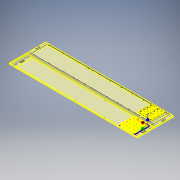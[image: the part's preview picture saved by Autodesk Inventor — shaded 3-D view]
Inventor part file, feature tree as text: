
AUTODESK INVENTOR PART (.ipt)
format: ipt  version: 2018.3 (Build 223284000, 284)  size: 9,961,472 bytes
history: native  units: in
note: dims shown in document units (in); Inventor stores cm internally (conversion verified against a paired STEP export)
features: other x145, extrude x13, projected_geometry x10, pattern_linear x5, hole x3, sketch x2
ambient origin geometry x8: Origin, YZ Plane, XZ Plane, XY Plane, X Axis, Y Axis, Z Axis, Center Point
bodies: Solid61 (feature_tree), Solid62 (feature_tree), Solid63 (feature_tree), Solid64 (feature_tree), Solid89 (feature_tree), Solid161 (feature_tree), Solid162 (feature_tree), Solid171 (feature_tree), Solid173 (feature_tree), Solid174 (feature_tree), Solid176 (feature_tree), Solid177 (feature_tree), Solid242 (feature_tree), Solid244 (feature_tree), Solid246 (feature_tree), Solid247 (feature_tree), Solid248 (feature_tree), Solid249 (feature_tree), Solid250 (feature_tree), Solid272 (feature_tree), Solid273 (feature_tree), Solid274 (feature_tree), Solid275 (feature_tree), Solid276 (feature_tree), Solid298 (feature_tree), Solid299 (feature_tree), Solid300 (feature_tree), Solid301 (feature_tree), Solid302 (feature_tree), Solid372 (feature_tree), Solid378 (feature_tree), Solid379 (feature_tree), Solid385 (feature_tree), Solid386 (feature_tree), Solid488 (feature_tree), Solid489 (feature_tree), Solid490 (feature_tree), Solid491 (feature_tree), Solid492 (feature_tree), Solid493 (feature_tree), Solid494 (feature_tree), Solid495 (feature_tree), Solid609 (feature_tree), Solid611 (feature_tree), Solid608 (feature_tree), Solid610 (feature_tree)
feature tree (178):
  other  "Fixture Assembly.iam"
  other  "Fixture Base.ipt:1"
  other  "Case Top Contour Fixture.ipt:1"
  other  "Case Top Contour Fixture.ipt:2"
  other  "Case Top Contour Fixture.ipt:3"
  other  "Case Top Contour Fixture.ipt:4"
  other  "Case Top Contour Fixture.ipt:5"
  other  "Case Top Contour Fixture.ipt:6"
  other  "Case Bottom Contour Fixture.ipt:16"
  other  "Case Top Pocket Fixture.ipt:1"
  other  "Case Bottom Pocket Fixture.ipt:1"
  other  "Case Top Pocket Fixture.ipt:3"
  other  "Case Top Pocket Fixture.ipt:4"
  other  "Case Top Pocket Fixture.ipt:5"
  other  "Case Top Pocket Fixture.ipt:6"
  other  "Case Top Pocket Fixture.ipt:7"
  other  "Case Bottom Contour Fixture.ipt:17"
  other  "Case Bottom Contour Fixture.ipt:18"
  other  "Case Bottom Contour Fixture.ipt:19"
  other  "Case Bottom Contour Fixture.ipt:20"
  other  "Case Bottom Contour Fixture.ipt:21"
  other  "Case Bottom Pocket Fixture.ipt:2"
  other  "Case Bottom Pocket Fixture.ipt:3"
  other  "Case Bottom Pocket Fixture.ipt:4"
  other  "Case Bottom Pocket Fixture.ipt:5"
  other  "Case Bottom Pocket Fixture.ipt:6"
  other  "Case Top Pocket Fixture.ipt:17"
  other  "Case Top Pocket Fixture.ipt:19"
  other  "Case Top Pocket Fixture.ipt:50"
  other  "Case Bottom Pocket Fixture.ipt:49"
  other  "Case Top Pocket Fixture.ipt:51"
  other  "Case Bottom Pocket Fixture.ipt:50"
  other  "Case Top Contour Fixture.ipt:7"
  other  "Case Bottom Contour Fixture.ipt:22"
  other  "Case Top Contour Fixture.ipt:8"
  other  "Case Bottom Contour Fixture.ipt:23"
  other  "Base Solid"
  other  "Pocket Registration Sketch"
  other  "Contour Registration Sketch"
  extrude  "Pocket Registration Hole"  Depth=0.3937in
  extrude  "Contour Registration Hole"  Depth=0.25in
  other  "Hold-down Plane"
  other  "Hold-down Sketch 1"
  other  "Hold-down Sketch 2"
  extrude  "Hold-down Pocket 1"  TaperAngle=0.0deg  [1 undecoded]
  extrude  "Hold-down Pocket 2"  TaperAngle=0.0deg  [1 undecoded]
  pattern_linear  "Hold-down Pocket Pattern"  Spacing1=0.25in  [1 undecoded]
  other  "Case Top Mount Sketch"
  extrude  "Case Top Mount Outer Extrusion"  Depth=0.55in
  extrude  "Case Top Mount Opening Extrusion"  Depth=0.75in TaperAngle=360.0deg
  extrude  "Case Bottom Mount Extrusion"  Depth=0.75in TaperAngle=0.0deg
  extrude  "Case Top Mount Ejection"  Depth=0.75in TaperAngle=0.0deg
  extrude  "Case Bottom Mount Ejection"  Depth=2.353in
  hole  "Case Bottom Vacuum Hole"  [1 undecoded]
  hole  "Case Top Long-grain Vacuum Hole"  [1 undecoded]
  hole  "Case Top End-grain Vacuum Hole"  [1 undecoded]
  pattern_linear  "Group Pattern"  Spacing1=0.25in  [1 undecoded]
  pattern_linear  "Group Fixture Pattern"  Spacing1=0.25in  [1 undecoded]
  other  "Partial Clean Sketch"
  extrude  "Extrusion43"  Depth=0.25in
  extrude  "Extrusion44"  Depth=0.75in
  pattern_linear  "Rectangular Pattern14"  Spacing1=10.0in  [1 undecoded]
  extrude  "Extrusion45"  Depth=0.75in
  extrude  "Extrusion46"  Depth=0.75in
  pattern_linear  "Rectangular Pattern15"  Spacing1=30.0in  [1 undecoded]
  other  "First Contour Top"
  other  "Origin Sketch"
  other  "Alignment Sketch_1"
  other  "3/16" Vacuum Drill Sketch"
  projected_geometry  "Projected Loop17"
  sketch  "Sketch496"  dims[d16=0.7874in d18=4.706in d29=0.3937in]
  other  "First Contour Bottom"
  other  "Alignment Sketch_56"
  other  "Peg Sketch_45"
  sketch  "Sketch509"  dims[d205=0.55in d206=0.25in d232=0.0in d233=0.0in d234=0.0in d235=0.0in d236=0.25in d237=0.55in d238=1.5748in d240=360.0deg d242=0.08in d243=0.0in d244=0.08in d245=0.0in d246=0.5in d247=0.75in d248=0.375in d249=0.25in d250=0.5635in d251=1.0in d252=0.8108in d253=0.1875in d254=0.75in d255=0.375in d256=0.25in d257=0.5635in d258=1.0in d259=0.8108in d260=0.125in d261=0.75in d262=0.375in d263=0.25in d264=0.5635in d265=1.0in d266=0.8108in d267=1.5748in d269=2.353in d372=0.25in d373=0.25in d374=0.25in d375=0.25in d376=0.25in d377=0.25in d378=10.0in d379=10.0in d380=10.0in d381=20.0in d382=30.0in d383=41.0in d384=10.0in d385=0.25in d390=1.0in d391=0.0in d393=1.0in d402=0.05in d403=0.0in d404=0.05in d405=0.0in d420=0.126in d436=0.025in d437=0.0in d438=3.1496in d440=10.25in d441=0.126in d442=0.025in d443=0.0in d444=0.3937in d446=10.25in d468=0.25in d469=0.25in d473=0.75in d475=1.5748in d477=360.0deg d481=0.25in d482=0.5in d483=0.0in d484=10.0in d485=0.25in d486=0.0in d487=0.5in d488=0.25in d489=0.25in d490=0.25in d491=0.125in d492=0.125in d493=0.0in d494=0.0in d499=0.25in d500=0.05in d501=0.0in d502=3.937in d504=1.0in d505=0.3937in d507=1.0in d509=0.126in d510=5.076in d511=0.126in d512=5.076in d513=0.015in d514=0.0in d515=0.015in d516=0.0in d517=6.2992in d519=5.06in d520=0.25in d521=0.75in d522=0.3818in d523=0.126in d524=7.198in d525=0.023in d526=0.025in d527=0.0in d528=2.7559in d530=7.75in d531=0.75in d532=0.126in d533=7.198in d534=0.7499in d535=0.015in d536=0.0in]
  other  "Pattern of Solid162:9"
  other  "Pattern of Solid162:11"
  other  "Pattern of Solid162:12"
  other  "Pattern of Solid162:14"
  other  "Pattern of Solid162:15"
  other  "New peg sketch_51"
  other  "Alignment Sketch"
  other  "3/16" Vacuum Drill Sketch_36"
  other  "Alignment Sketch_63"
  other  "New peg sketch_53"
  other  "Alignment Sketch_65"
  other  "3/16" Vacuum Drill Sketch_38"
  other  "New peg sketch_54"
  other  "Alignment Sketch_66"
  other  "3/16" Vacuum Drill Sketch_39"
  other  "New peg sketch_55"
  other  "Alignment Sketch_67"
  other  "3/16" Vacuum Drill Sketch_40"
  other  "New peg sketch_56"
  other  "Alignment Sketch_68"
  other  "3/16" Vacuum Drill Sketch_41"
  other  "New peg sketch_57"
  other  "Alignment Sketch_69"
  other  "3/16" Vacuum Drill Sketch_42"
  other  "Alignment Sketch_73"
  other  "Peg Sketch_46"
  other  "Alignment Sketch_74"
  other  "Peg Sketch_47"
  other  "Alignment Sketch_75"
  other  "Peg Sketch_48"
  other  "Alignment Sketch_76"
  other  "Peg Sketch_49"
  other  "Alignment Sketch_77"
  other  "Peg Sketch_50"
  other  "Alignment Sketch_99"
  other  "Alignment Sketch_100"
  other  "Alignment Sketch_101"
  other  "Alignment Sketch_102"
  other  "Alignment Sketch_103"
  other  "Alignment Sketch_113"
  other  "Alignment Sketch_117"
  other  "Pattern of Solid161:26"
  other  "Pattern of Solid161:30"
  other  "Pattern of Solid161:31"
  other  "Pattern of Solid161:35"
  other  "Pattern of Solid161:36"
  other  "Inner Narrowing Sketch"
  other  "Opening Narrowing Sketch"
  other  "Inner Narrowing Sketch_1"
  other  "Opening Narrowing Sketch_1"
  other  "Inner Narrowing Sketch_2"
  other  "Opening Narrowing Sketch_2"
  other  "Inner Narrowing Sketch_3"
  other  "Opening Narrowing Sketch_3"
  other  "Inner Narrowing Sketch_4"
  other  "Opening Narrowing Sketch_4"
  other  "Inner Narrowing Sketch_5"
  other  "Opening Narrowing Sketch_5"
  other  "New peg sketch"
  other  "New peg sketch_58"
  other  "Alignment Sketch_118"
  other  "New peg sketch_59"
  other  "Alignment Sketch_119"
  other  "New peg sketch_60"
  other  "Alignment Sketch_120"
  other  "New peg sketch_61"
  other  "Alignment Sketch_121"
  other  "New peg sketch_62"
  other  "Alignment Sketch_122"
  projected_geometry  "Projected Loop42"
  projected_geometry  "Projected Loop43"
  projected_geometry  "Projected Loop44"
  projected_geometry  "Projected Loop45"
  projected_geometry  "Projected Loop46"
  projected_geometry  "Projected Loop47"
  projected_geometry  "Projected Loop48"
  projected_geometry  "Projected Loop49"
  projected_geometry  "Projected Loop50"
  other  "Base Sketch"
  other  "New peg sketch_63"
  other  "Alignment Sketch_123"
  other  "3/16" Vacuum Drill Sketch_43"
  other  "Alignment Sketch_124"
  other  "New peg sketch_64"
  other  "Alignment Sketch_125"
  other  "3/16" Vacuum Drill Sketch_44"
  other  "Alignment Sketch_126"
  other  "New peg sketch_65"
  other  "Alignment Sketch_127"
  other  "Inner Narrowing Sketch_6"
  other  "Opening Narrowing Sketch_6"
  other  "Alignment Sketch_128"
  other  "Peg Sketch"
  other  "New peg sketch_66"
  other  "Alignment Sketch_129"
  other  "Inner Narrowing Sketch_7"
  other  "Opening Narrowing Sketch_7"
  other  "Alignment Sketch_130"
  other  "Peg Sketch_51"
  other  "Pattern of Solid162:40"
  other  "Pattern of Solid162:41"
  other  "Pattern of Solid161:42"
  other  "Pattern of Solid161:43"
note: 10 required parameter values undecoded (feature->parameter linkage not recoverable at this tier; creation-order binding heuristic only, values carry confidence <= 0.55)
